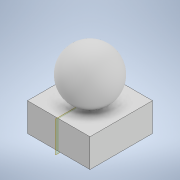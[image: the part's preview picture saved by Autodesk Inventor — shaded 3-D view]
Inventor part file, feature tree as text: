
AUTODESK INVENTOR PART (.ipt)
format: ipt  version: 2021 (Build 250183000, 183)  size: 131,072 bytes
history: native  units: in
note: dims shown in document units (in); Inventor stores cm internally (conversion verified against a paired STEP export)
features: sketch x2, extrude x1, plane x1, revolve x1
ambient origin geometry x8: Origin, YZ Plane, XZ Plane, XY Plane, X Axis, Y Axis, Z Axis, Center Point
bodies: Body1 (feature_tree)
feature tree (5):
  extrude  "Extrusion3"  Depth=0.8661in
  plane  "Work Plane1"
  revolve  "Revolution2"  [1 undecoded]
  sketch  "Sketch6"  dims[d18=0.8661in d19=0.8661in]
  sketch  "Sketch8"  dims[d20=0.3937in d21=0.0in d27=-0.4331in d30=0.315in d31=0.7087in d32=360.0deg]
note: 1 required parameter value undecoded (feature->parameter linkage not recoverable at this tier; creation-order binding heuristic only, values carry confidence <= 0.55)
